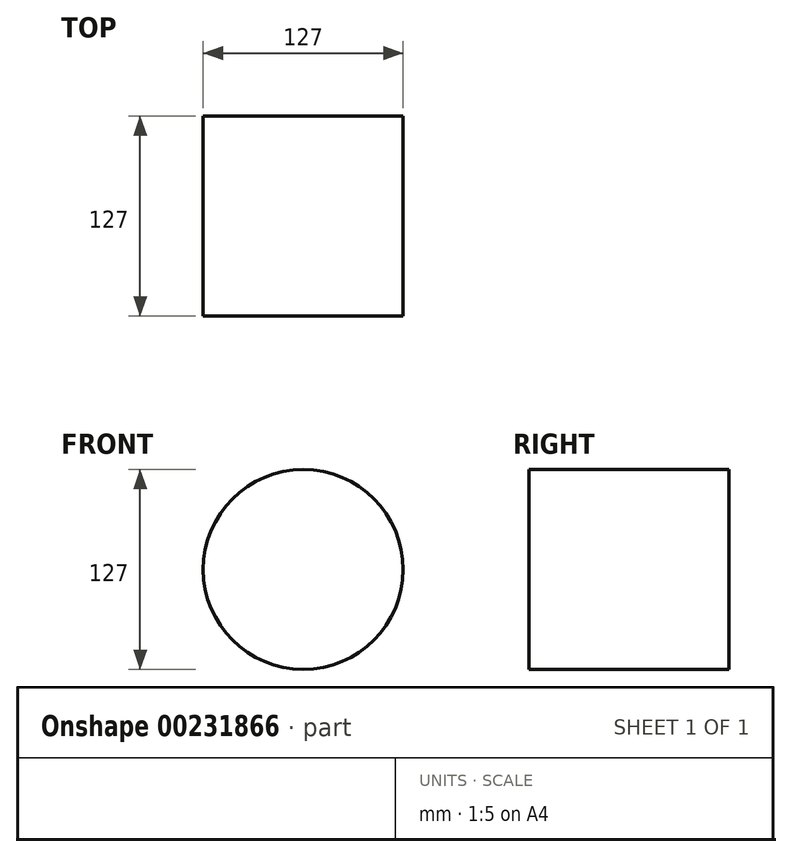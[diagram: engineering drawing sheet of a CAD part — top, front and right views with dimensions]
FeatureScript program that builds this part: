
annotation { "Feature Type Name" : "Feature", "Feature Type Description" : "" }
export const myFeature = defineFeature(function(context is Context, id is Id, definition is map)
    precondition{}
    {
        {
            var Q0;
            Q0=qCreatedBy(makeId("Front.planeOp"),FACE);
            var sketch = newSketch(context, id + "F0", { "sketchPlane" : qUnion([Q0])});
            skCircle(sketch, "E0", {"center": v(0, 0) * mm, "radius": 63.5 * mm});
            skSolve(sketch);
        }
        {
            var Q0;
            Q0 = qSketchRegion(id + "F0", true);
            extrude(context, id + "F1", {"entities" : qUnion([Q0]), "depth" : 127 * mm});
        }
    });
